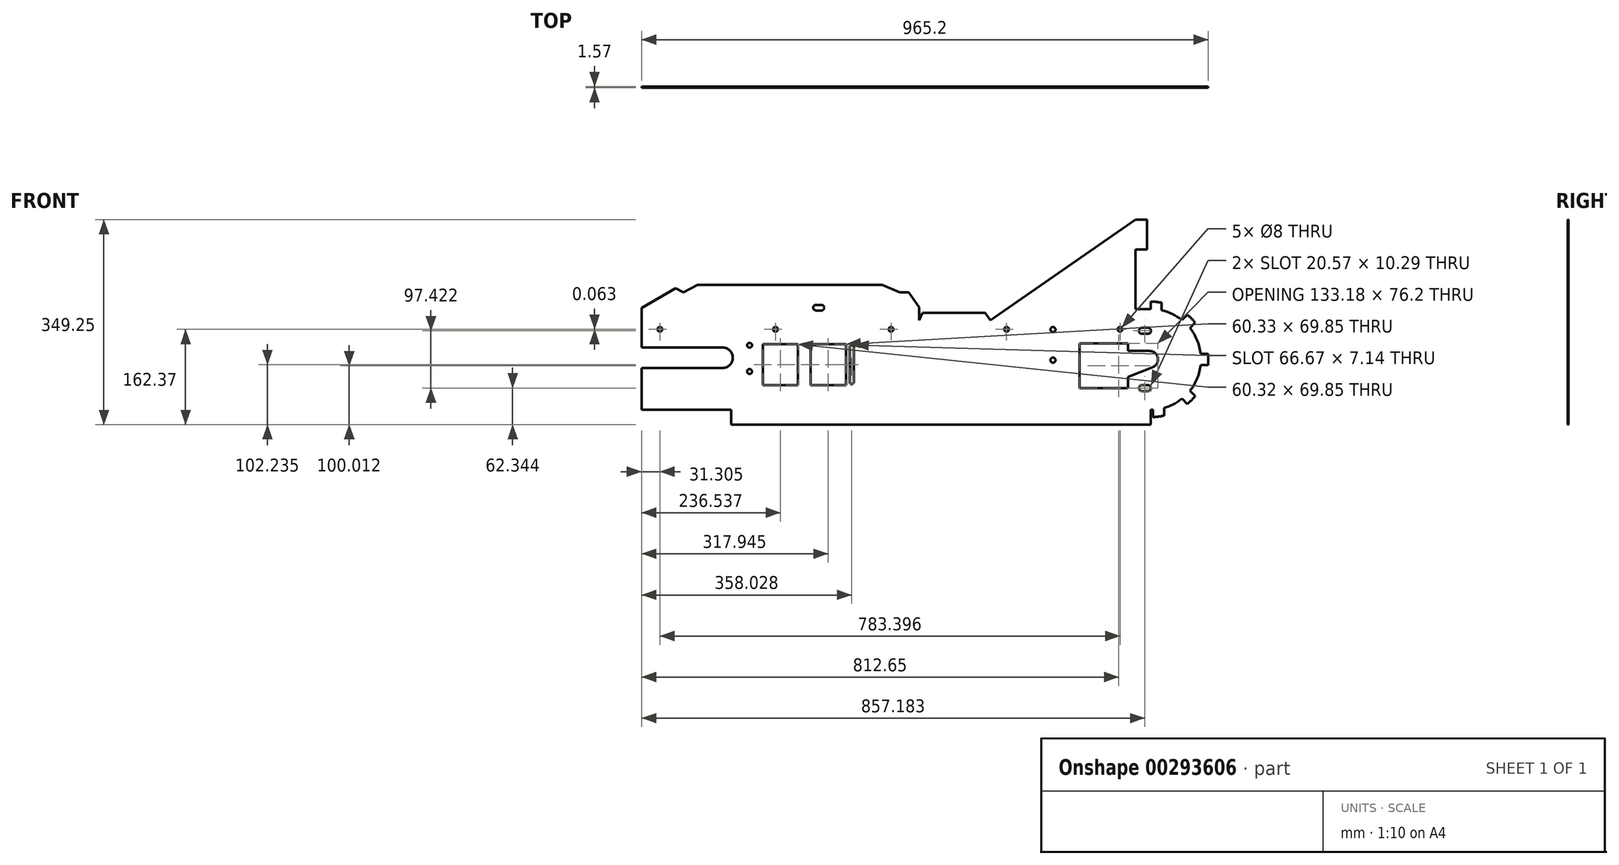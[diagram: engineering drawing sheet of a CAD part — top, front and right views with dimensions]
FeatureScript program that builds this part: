
annotation { "Feature Type Name" : "Feature", "Feature Type Description" : "" }
export const myFeature = defineFeature(function(context is Context, id is Id, definition is map)
    precondition{}
    {
        {
            var Q0;
            Q0=qCreatedBy(makeId("Front.planeOp"),FACE);
            var sketch = newSketch(context, id + "F0", { "sketchPlane" : qUnion([Q0])});
            skLineSegment(sketch, "E0", {"start": v(0, 0) * mm, "end": v(866.78, 0) * mm});
            skLineSegment(sketch, "E1", {"start": v(0, 71.12) * mm, "end": v(138.11, 71.12) * mm});
            skLineSegment(sketch, "E2", {"start": v(138.11, 106.05) * mm, "end": v(0, 106.05) * mm});
            skLineSegment(sketch, "E3", {"start": v(0, 106.05) * mm, "end": v(0, 158.75) * mm});
            skLineSegment(sketch, "E4", {"start": v(0, 158.75) * mm, "end": v(71.5, 200.03) * mm});
            skLineSegment(sketch, "E5", {"start": v(71.5, 200.03) * mm, "end": v(439.73, 200.03) * mm});
            skLineSegment(sketch, "E6", {"start": v(439.73, 200.03) * mm, "end": v(473.08, 152.4) * mm});
            skLineSegment(sketch, "E7", {"start": v(473.08, 152.4) * mm, "end": v(593.73, 152.4) * mm});
            skLineSegment(sketch, "E8", {"start": v(593.73, 152.4) * mm, "end": v(841.38, 323.85) * mm});
            skLineSegment(sketch, "E9", {"start": v(841.38, 323.85) * mm, "end": v(841.38, 171.45) * mm});
            skPoint(sketch, "E10", {"position": v(866.78, 85.73) * mm});
            skArc(sketch, "E11", {"start": v(866.78, 0) * mm, "mid": v(952.5, 85.73) * mm, "end": v(866.78, 171.45) * mm});
            skLineSegment(sketch, "E12", {"start": v(866.78, 171.45) * mm, "end": v(751.67, 171.45) * mm});
            skPoint(sketch, "E13", {"position": v(138.11, 88.58) * mm});
            skPoint(sketch, "E13.positionSnap0", {"position": v(155.58, 88.58) * mm});
            skArc(sketch, "E14", {"start": v(138.11, 71.12) * mm, "mid": v(155.58, 88.58) * mm, "end": v(138.11, 106.04) * mm});
            skLineSegment(sketch, "E15", {"start": v(206.38, 88.58) * mm, "end": v(206.38, 41.91) * mm});
            skLineSegment(sketch, "E16", {"start": v(206.38, 41.91) * mm, "end": v(266.7, 41.91) * mm});
            skLineSegment(sketch, "E17", {"start": v(266.7, 41.91) * mm, "end": v(266.7, 111.76) * mm});
            skLineSegment(sketch, "E18", {"start": v(266.7, 111.76) * mm, "end": v(206.38, 111.76) * mm});
            skLineSegment(sketch, "E19", {"start": v(206.38, 111.76) * mm, "end": v(206.38, 88.58) * mm});
            skLineSegment(sketch, "E20.bottom", {"start": v(287.78, 41.91) * mm, "end": v(348.1, 41.91) * mm});
            skLineSegment(sketch, "E20.top", {"start": v(287.78, 111.76) * mm, "end": v(348.1, 111.76) * mm});
            skLineSegment(sketch, "E20.left", {"start": v(287.78, 41.91) * mm, "end": v(287.78, 111.76) * mm});
            skLineSegment(sketch, "E20.right", {"start": v(348.1, 41.91) * mm, "end": v(348.1, 111.76) * mm});
            skArc(sketch, "E21", {"start": v(354.46, 47.07) * mm, "mid": v(358.08, 43.5) * mm, "end": v(361.6, 47.17) * mm});
            skArc(sketch, "E22", {"start": v(361.6, 106.5) * mm, "mid": v(358.08, 110.17) * mm, "end": v(354.46, 106.6) * mm});
            skLineSegment(sketch, "E23", {"start": v(361.6, 106.7) * mm, "end": v(361.6, 47.07) * mm});
            skLineSegment(sketch, "E24", {"start": v(0, 0) * mm, "end": v(0, 71.12) * mm});
            skLineSegment(sketch, "E25", {"start": v(354.46, 47.07) * mm, "end": v(354.46, 106.6) * mm});
            skPoint(sketch, "E26.orphan", {"position": v(155.58, 106.05) * mm});
            skPoint(sketch, "E27.orphan", {"position": v(155.57, 71.12) * mm});
            skLineSegment(sketch, "E28.bottom", {"start": v(746.06, 36.51) * mm, "end": v(828.6, 36.51) * mm});
            skLineSegment(sketch, "E28.top", {"start": v(746.06, 112.71) * mm, "end": v(828.6, 112.71) * mm});
            skLineSegment(sketch, "E28.left", {"start": v(746.06, 36.51) * mm, "end": v(746.06, 112.71) * mm});
            skLineSegment(sketch, "E28.right", {"start": v(828.6, 36.51) * mm, "end": v(828.6, 55.56) * mm});
            skLineSegment(sketch, "E29", {"start": v(828.6, 100.01) * mm, "end": v(865.12, 100.01) * mm});
            skPoint(sketch, "E30", {"position": v(828.6, 55.56) * mm});
            skPoint(sketch, "E31", {"position": v(865.12, 85.73) * mm});
            skArc(sketch, "E32", {"start": v(870.47, 72.48) * mm, "mid": v(879.15, 88.45) * mm, "end": v(865.12, 100.01) * mm});
            skLineSegment(sketch, "E33", {"start": v(828.6, 55.56) * mm, "end": v(870.47, 72.48) * mm});
            skLineSegment(sketch, "E34.trimOffspring", {"start": v(828.6, 100.01) * mm, "end": v(828.6, 112.71) * mm});
            skLineSegment(sketch, "E35", {"start": v(152.4, 0) * mm, "end": v(152.4, -25.4) * mm});
            skLineSegment(sketch, "E36", {"start": v(152.4, -25.4) * mm, "end": v(866.78, -25.4) * mm});
            skLineSegment(sketch, "E37", {"start": v(866.78, -25.4) * mm, "end": v(866.78, 0) * mm});
            skLineSegment(sketch, "E38", {"start": v(71.5, 200.03) * mm, "end": v(95.54, 212.72) * mm});
            skLineSegment(sketch, "E39", {"start": v(95.54, 212.72) * mm, "end": v(410.03, 212.72) * mm});
            skLineSegment(sketch, "E40", {"start": v(410.03, 212.72) * mm, "end": v(439.73, 200.03) * mm});
            skArc(sketch, "E41.0", {"start": v(871, -12.6) * mm, "mid": v(880.5, -11.74) * mm, "end": v(889.87, -9.95) * mm});
            skLineSegment(sketch, "E42", {"start": v(866.78, 184.15) * mm, "end": v(866.78, 171.45) * mm});
            skLineSegment(sketch, "E43", {"start": v(885.7, 169.33) * mm, "end": v(885.74, 182.3) * mm});
            skLineSegment(sketch, "E44", {"start": v(951.97, 95.25) * mm, "end": v(964.74, 95.25) * mm});
            skLineSegment(sketch, "E45", {"start": v(951.97, 76.2) * mm, "end": v(964.74, 76.2) * mm});
            skLineSegment(sketch, "E46", {"start": v(871, 0.1) * mm, "end": v(871, -12.6) * mm});
            skLineSegment(sketch, "E47", {"start": v(889.81, 3.15) * mm, "end": v(889.87, -9.95) * mm});
            skLineSegment(sketch, "E48", {"start": v(866.78, 85.73) * mm, "end": v(1018.53, 85.73) * mm});
            skLineSegment(sketch, "E49", {"start": v(866.78, 85.72) * mm, "end": v(977.94, 196.9) * mm});
            skLineSegment(sketch, "E50", {"start": v(866.78, 85.73) * mm, "end": v(952.5, 0) * mm});
            skLineSegment(sketch, "E51", {"start": v(920.28, 152.7) * mm, "end": v(929.31, 161.73) * mm});
            skLineSegment(sketch, "E52", {"start": v(933.75, 139.23) * mm, "end": v(942.78, 148.26) * mm});
            skLineSegment(sketch, "E53", {"start": v(933.75, 32.22) * mm, "end": v(942.78, 23.19) * mm});
            skLineSegment(sketch, "E54", {"start": v(920.28, 18.75) * mm, "end": v(929.31, 9.72) * mm});
            skArc(sketch, "E55.trimOffspring", {"start": v(929.31, 9.72) * mm, "mid": v(936.37, 16.13) * mm, "end": v(942.78, 23.19) * mm});
            skArc(sketch, "E56.trimOffspring", {"start": v(964.74, 76.2) * mm, "mid": v(965.08, 80.96) * mm, "end": v(965.2, 85.73) * mm});
            skArc(sketch, "E57.trimOffspring", {"start": v(942.78, 148.26) * mm, "mid": v(936.37, 155.32) * mm, "end": v(929.31, 161.73) * mm});
            skArc(sketch, "E58.trimOffspring", {"start": v(885.74, 182.3) * mm, "mid": v(876.3, 183.69) * mm, "end": v(866.78, 184.15) * mm});
            skLineSegment(sketch, "E59.0", {"start": v(0, 173.41) * mm, "end": v(57.89, 206.84) * mm});
            skLineSegment(sketch, "E60.0", {"start": v(455.23, 200.03) * mm, "end": v(473.08, 174.54) * mm});
            skLineSegment(sketch, "E61.1", {"start": v(478.15, 165.1) * mm, "end": v(584.93, 165.1) * mm});
            skLineSegment(sketch, "E62", {"start": v(71.5, 200.03) * mm, "end": v(57.89, 206.84) * mm});
            skLineSegment(sketch, "E63", {"start": v(0, 158.75) * mm, "end": v(0, 173.41) * mm});
            skLineSegment(sketch, "E64", {"start": v(439.73, 200.03) * mm, "end": v(455.23, 200.03) * mm});
            skLineSegment(sketch, "E65", {"start": v(473.08, 152.4) * mm, "end": v(473.08, 174.54) * mm});
            skLineSegment(sketch, "E66", {"start": v(473.08, 152.4) * mm, "end": v(478.15, 165.1) * mm});
            skLineSegment(sketch, "E67", {"start": v(593.73, 152.4) * mm, "end": v(584.93, 165.1) * mm});
            skLineSegment(sketch, "E68", {"start": v(593.73, 152.4) * mm, "end": v(593.73, 167.85) * mm});
            skLineSegment(sketch, "E69.bottom", {"start": v(841.38, 323.85) * mm, "end": v(860.43, 323.85) * mm});
            skLineSegment(sketch, "E69.top", {"start": v(841.38, 273.05) * mm, "end": v(860.43, 273.05) * mm});
            skLineSegment(sketch, "E69.left", {"start": v(841.38, 323.85) * mm, "end": v(841.38, 273.05) * mm});
            skLineSegment(sketch, "E69.right", {"start": v(860.43, 323.85) * mm, "end": v(860.43, 273.05) * mm});
            skLineSegment(sketch, "E70.bottom", {"start": v(841.38, 171.45) * mm, "end": v(860.43, 171.45) * mm});
            skLineSegment(sketch, "E70.top", {"start": v(841.38, 222.25) * mm, "end": v(860.43, 222.25) * mm});
            skLineSegment(sketch, "E70.left", {"start": v(841.38, 171.45) * mm, "end": v(841.38, 222.25) * mm});
            skLineSegment(sketch, "E70.right", {"start": v(860.43, 171.45) * mm, "end": v(860.43, 222.25) * mm});
            skCircle(sketch, "E71", {"center": v(184.09, 65.09) * mm, "radius": 4.13 * mm});
            skCircle(sketch, "E72", {"center": v(184.09, 109.82) * mm, "radius": 4.13 * mm});
            skCircle(sketch, "E73", {"center": v(228.08, 136.97) * mm, "radius": 4 * mm});
            skLineSegment(sketch, "E74", {"start": v(228.08, 136.97) * mm, "end": v(24.96, 136.97) * mm});
            skCircle(sketch, "E75", {"center": v(31.3, 136.97) * mm, "radius": 4 * mm});
            skLineSegment(sketch, "E76", {"start": v(228.08, 136.97) * mm, "end": v(670.87, 136.97) * mm});
            skCircle(sketch, "E77", {"center": v(424.85, 136.97) * mm, "radius": 4 * mm});
            skCircle(sketch, "E78", {"center": v(621.63, 136.97) * mm, "radius": 4 * mm});
            skCircle(sketch, "E79", {"center": v(306.45, 173.86) * mm, "radius": 4.7 * mm});
            skCircle(sketch, "E80", {"center": v(297.05, 173.86) * mm, "radius": 4.7 * mm});
            skLineSegment(sketch, "E81", {"start": v(306.45, 178.56) * mm, "end": v(297.05, 178.56) * mm});
            skLineSegment(sketch, "E82", {"start": v(306.45, 169.16) * mm, "end": v(297.05, 169.16) * mm});
            skCircle(sketch, "E83", {"center": v(852.04, 134.37) * mm, "radius": 5.14 * mm});
            skCircle(sketch, "E84", {"center": v(852.04, 36.94) * mm, "radius": 5.14 * mm});
            skCircle(sketch, "E85", {"center": v(814.7, 137.03) * mm, "radius": 4 * mm});
            skCircle(sketch, "E86", {"center": v(862.33, 134.37) * mm, "radius": 5.14 * mm});
            skCircle(sketch, "E87", {"center": v(862.33, 36.94) * mm, "radius": 5.14 * mm});
            skLineSegment(sketch, "E88", {"start": v(862.33, 139.5) * mm, "end": v(852.04, 139.5) * mm});
            skLineSegment(sketch, "E89", {"start": v(862.33, 129.22) * mm, "end": v(852.04, 129.22) * mm});
            skLineSegment(sketch, "E90", {"start": v(862.33, 42.09) * mm, "end": v(852.04, 42.09) * mm});
            skLineSegment(sketch, "E91", {"start": v(862.33, 31.8) * mm, "end": v(852.04, 31.8) * mm});
            skCircle(sketch, "E92", {"center": v(700.6, 136.59) * mm, "radius": 4.32 * mm});
            skCircle(sketch, "E93", {"center": v(700.6, 84.52) * mm, "radius": 4.32 * mm});
            skLineSegment(sketch, "E94", {"start": v(965.2, 85.73) * mm, "end": v(964.74, 95.25) * mm});
            skSolve(sketch);
        }
        {
            var Q0;
            Q0=makeQuery(id+"F0.imprint","IMPRINT",FACE,{"disambiguationData":[TD([[makeQuery(id+"F0.imprint","IMPRINT",EDGE,{"derivedFrom":sQuery(id+"F0.wireOp",EDGE,"E1")}),-1.0]])]});
            var Q1;
            {var subQ0=sQuery(id+"F0.wireOp",EDGE,"E11");var subQ8=makeQuery(id+"F0.imprint","INTERSECT",VERTEX,{"derivedFrom":[subQ0,sQuery(id+"F0.wireOp",EDGE,"E44")]});Q1=makeQuery(id+"F0.imprint","IMPRINT",FACE,{"disambiguationData":[TD([[makeQuery(id+"F0.imprint","IMPRINT",EDGE,{"disambiguationData":[TD([[subQ8,1.0]])],"derivedFrom":subQ0}),1.0]])]});}
            var Q2;
            {var subQ5=sQuery(id+"F0.wireOp",EDGE,"E11");var subQ6=makeQuery(id+"F0.imprint","INTERSECT",VERTEX,{"derivedFrom":[subQ5,sQuery(id+"F0.wireOp",EDGE,"E53")]});Q2=makeQuery(id+"F0.imprint","IMPRINT",FACE,{"disambiguationData":[TD([[makeQuery(id+"F0.imprint","IMPRINT",EDGE,{"disambiguationData":[TD([[subQ6,1.0]])],"derivedFrom":subQ5}),1.0]])]});}
            var Q3;
            {var subQ0=sQuery(id+"F0.wireOp",EDGE,"E42");Q3=makeQuery(id+"F0.imprint","IMPRINT",FACE,{"disambiguationData":[TD([[makeQuery(id+"F0.imprint","IMPRINT",EDGE,{"derivedFrom":subQ0}),1.0]])]});}
            var Q4;
            Q4=makeQuery(id+"F0.imprint","IMPRINT",FACE,{"disambiguationData":[TD([[makeQuery(id+"F0.imprint","IMPRINT",EDGE,{"derivedFrom":sQuery(id+"F0.wireOp",EDGE,"E70.bottom")}),1.0]])]});
            var Q5;
            Q5=makeQuery(id+"F0.imprint","IMPRINT",FACE,{"disambiguationData":[TD([[makeQuery(id+"F0.imprint","IMPRINT",EDGE,{"derivedFrom":sQuery(id+"F0.wireOp",EDGE,"E69.bottom")}),-1.0]])]});
            var Q6;
            {var subQ0=sQuery(id+"F0.wireOp",EDGE,"E51");Q6=makeQuery(id+"F0.imprint","IMPRINT",FACE,{"disambiguationData":[TD([[makeQuery(id+"F0.imprint","IMPRINT",EDGE,{"derivedFrom":subQ0}),-1.0]])]});}
            var Q7;
            {var subQ0=sQuery(id+"F0.wireOp",EDGE,"E52");Q7=makeQuery(id+"F0.imprint","IMPRINT",FACE,{"disambiguationData":[TD([[makeQuery(id+"F0.imprint","IMPRINT",EDGE,{"derivedFrom":subQ0}),1.0]])]});}
            var Q8;
            {var subQ0=sQuery(id+"F0.wireOp",EDGE,"E44");Q8=makeQuery(id+"F0.imprint","IMPRINT",FACE,{"disambiguationData":[TD([[makeQuery(id+"F0.imprint","IMPRINT",EDGE,{"derivedFrom":subQ0}),-1.0]])]});}
            var Q9;
            {var subQ0=sQuery(id+"F0.wireOp",EDGE,"E45");Q9=makeQuery(id+"F0.imprint","IMPRINT",FACE,{"disambiguationData":[TD([[makeQuery(id+"F0.imprint","IMPRINT",EDGE,{"derivedFrom":subQ0}),1.0]])]});}
            var Q10;
            {var subQ0=sQuery(id+"F0.wireOp",EDGE,"E53");Q10=makeQuery(id+"F0.imprint","IMPRINT",FACE,{"disambiguationData":[TD([[makeQuery(id+"F0.imprint","IMPRINT",EDGE,{"derivedFrom":subQ0}),-1.0]])]});}
            var Q11;
            {var subQ0=sQuery(id+"F0.wireOp",EDGE,"E54");Q11=makeQuery(id+"F0.imprint","IMPRINT",FACE,{"disambiguationData":[TD([[makeQuery(id+"F0.imprint","IMPRINT",EDGE,{"derivedFrom":subQ0}),1.0]])]});}
            var Q12;
            Q12=makeQuery(id+"F0.imprint","IMPRINT",FACE,{"disambiguationData":[TD([[makeQuery(id+"F0.imprint","IMPRINT",EDGE,{"derivedFrom":sQuery(id+"F0.wireOp",EDGE,"E41.0")}),1.0]])]});
            var Q13;
            {var subQ2=sQuery(id+"F0.wireOp",EDGE,"E35");Q13=makeQuery(id+"F0.imprint","IMPRINT",FACE,{"disambiguationData":[TD([[makeQuery(id+"F0.imprint","IMPRINT",EDGE,{"derivedFrom":subQ2}),1.0]])]});}
            var Q14;
            Q14=makeQuery(id+"F0.imprint","IMPRINT",FACE,{"disambiguationData":[TD([[makeQuery(id+"F0.imprint","IMPRINT",EDGE,{"derivedFrom":sQuery(id+"F0.wireOp",EDGE,"E7")}),1.0]])]});
            var Q15;
            Q15=makeQuery(id+"F0.imprint","IMPRINT",FACE,{"disambiguationData":[TD([[makeQuery(id+"F0.imprint","IMPRINT",EDGE,{"derivedFrom":sQuery(id+"F0.wireOp",EDGE,"E6")}),1.0]])]});
            var Q16;
            Q16=makeQuery(id+"F0.imprint","IMPRINT",FACE,{"disambiguationData":[TD([[makeQuery(id+"F0.imprint","IMPRINT",EDGE,{"derivedFrom":sQuery(id+"F0.wireOp",EDGE,"E5")}),1.0]])]});
            var Q17;
            Q17=makeQuery(id+"F0.imprint","IMPRINT",FACE,{"disambiguationData":[TD([[makeQuery(id+"F0.imprint","IMPRINT",EDGE,{"derivedFrom":sQuery(id+"F0.wireOp",EDGE,"E4")}),1.0]])]});
            extrude(context, id + "F1", {"entities" : qUnion([Q0, Q1, Q2, Q3, Q4, Q5, Q6, Q7, Q8, Q9, Q10, Q11, Q12, Q13, Q14, Q15, Q16, Q17]), "depth" : 1.57 * mm});
        }
        {
            var Q0;
            Q0=makeQuery(id+"F1.opExtrude","CAP_FACE",FACE,{"disambiguationData":[OSD([sQuery(id+"F0.wireOp",EDGE,"E0"),sQuery(id+"F0.wireOp",EDGE,"E1"),sQuery(id+"F0.wireOp",EDGE,"E2"),sQuery(id+"F0.wireOp",EDGE,"E3"),sQuery(id+"F0.wireOp",EDGE,"E8"),sQuery(id+"F0.wireOp",EDGE,"E9"),sQuery(id+"F0.wireOp",EDGE,"E11"),sQuery(id+"F0.wireOp",EDGE,"E12"),sQuery(id+"F0.wireOp",EDGE,"E14"),sQuery(id+"F0.wireOp",EDGE,"E15"),sQuery(id+"F0.wireOp",EDGE,"E16"),sQuery(id+"F0.wireOp",EDGE,"E17"),sQuery(id+"F0.wireOp",EDGE,"E18"),sQuery(id+"F0.wireOp",EDGE,"E19"),sQuery(id+"F0.wireOp",EDGE,"E20.bottom"),sQuery(id+"F0.wireOp",EDGE,"E20.top"),sQuery(id+"F0.wireOp",EDGE,"E20.left"),sQuery(id+"F0.wireOp",EDGE,"E20.right"),sQuery(id+"F0.wireOp",EDGE,"E21"),sQuery(id+"F0.wireOp",EDGE,"E22"),sQuery(id+"F0.wireOp",EDGE,"E23"),sQuery(id+"F0.wireOp",EDGE,"E24"),sQuery(id+"F0.wireOp",EDGE,"E25"),sQuery(id+"F0.wireOp",EDGE,"E28.bottom"),sQuery(id+"F0.wireOp",EDGE,"E28.top"),sQuery(id+"F0.wireOp",EDGE,"E28.left"),sQuery(id+"F0.wireOp",EDGE,"E28.right"),sQuery(id+"F0.wireOp",EDGE,"E29"),sQuery(id+"F0.wireOp",EDGE,"E32"),sQuery(id+"F0.wireOp",EDGE,"E33"),sQuery(id+"F0.wireOp",EDGE,"E34.trimOffspring"),sQuery(id+"F0.wireOp",EDGE,"E35"),sQuery(id+"F0.wireOp",EDGE,"E36"),sQuery(id+"F0.wireOp",EDGE,"E37"),sQuery(id+"F0.wireOp",EDGE,"E38"),sQuery(id+"F0.wireOp",EDGE,"E39"),sQuery(id+"F0.wireOp",EDGE,"E40"),sQuery(id+"F0.wireOp",EDGE,"E41.0"),sQuery(id+"F0.wireOp",EDGE,"E42"),sQuery(id+"F0.wireOp",EDGE,"E43"),sQuery(id+"F0.wireOp",EDGE,"E44"),sQuery(id+"F0.wireOp",EDGE,"E45"),sQuery(id+"F0.wireOp",EDGE,"E46"),sQuery(id+"F0.wireOp",EDGE,"E47"),sQuery(id+"F0.wireOp",EDGE,"E51"),sQuery(id+"F0.wireOp",EDGE,"E52"),sQuery(id+"F0.wireOp",EDGE,"E53"),sQuery(id+"F0.wireOp",EDGE,"E54"),sQuery(id+"F0.wireOp",EDGE,"E55.trimOffspring"),sQuery(id+"F0.wireOp",EDGE,"E56.trimOffspring"),sQuery(id+"F0.wireOp",EDGE,"E57.trimOffspring"),sQuery(id+"F0.wireOp",EDGE,"E58.trimOffspring"),sQuery(id+"F0.wireOp",EDGE,"E59.0"),sQuery(id+"F0.wireOp",EDGE,"E60.0"),sQuery(id+"F0.wireOp",EDGE,"E61.1"),sQuery(id+"F0.wireOp",EDGE,"E62"),sQuery(id+"F0.wireOp",EDGE,"E63"),sQuery(id+"F0.wireOp",EDGE,"E64"),sQuery(id+"F0.wireOp",EDGE,"E65"),sQuery(id+"F0.wireOp",EDGE,"E66"),sQuery(id+"F0.wireOp",EDGE,"E67"),sQuery(id+"F0.wireOp",EDGE,"E69.bottom"),sQuery(id+"F0.wireOp",EDGE,"E69.top"),sQuery(id+"F0.wireOp",EDGE,"E69.right"),sQuery(id+"F0.wireOp",EDGE,"E70.top"),sQuery(id+"F0.wireOp",EDGE,"E70.right"),sQuery(id+"F0.wireOp",EDGE,"E71"),sQuery(id+"F0.wireOp",EDGE,"E72"),sQuery(id+"F0.wireOp",EDGE,"E73"),sQuery(id+"F0.wireOp",EDGE,"E75"),sQuery(id+"F0.wireOp",EDGE,"E77"),sQuery(id+"F0.wireOp",EDGE,"E78"),sQuery(id+"F0.wireOp",EDGE,"E79"),sQuery(id+"F0.wireOp",EDGE,"E80"),sQuery(id+"F0.wireOp",EDGE,"E81"),sQuery(id+"F0.wireOp",EDGE,"E82"),sQuery(id+"F0.wireOp",EDGE,"E83"),sQuery(id+"F0.wireOp",EDGE,"E84"),sQuery(id+"F0.wireOp",EDGE,"E85"),sQuery(id+"F0.wireOp",EDGE,"E86"),sQuery(id+"F0.wireOp",EDGE,"E87"),sQuery(id+"F0.wireOp",EDGE,"E88"),sQuery(id+"F0.wireOp",EDGE,"E89"),sQuery(id+"F0.wireOp",EDGE,"E90"),sQuery(id+"F0.wireOp",EDGE,"E91"),sQuery(id+"F0.wireOp",EDGE,"E92"),sQuery(id+"F0.wireOp",EDGE,"E93"),sQuery(id+"F0.wireOp",EDGE,"E94")])],"isStart":false});
            var sketch = newSketch(context, id + "F2", { "sketchPlane" : qUnion([Q0])});
            skLineSegment(sketch, "E95", {"start": v(860.43, 171.45) * mm, "end": v(841.38, 171.45) * mm});
            skLineSegment(sketch, "E96", {"start": v(841.38, 171.45) * mm, "end": v(841.38, 173.02) * mm});
            skLineSegment(sketch, "E97", {"start": v(841.38, 173.02) * mm, "end": v(860.43, 173.02) * mm});
            skLineSegment(sketch, "E98", {"start": v(860.43, 173.02) * mm, "end": v(860.43, 171.45) * mm});
            skSolve(sketch);
        }
        {
            var Q0;
            Q0=makeQuery(id+"F2.imprint","IMPRINT",FACE,{"disambiguationData":[TD([[makeQuery(id+"F2.imprint","IMPRINT",EDGE,{"derivedFrom":sQuery(id+"F2.wireOp",EDGE,"E95")}),-1.0]])]});
            extrude(context, id + "F3", {"entities" : qUnion([Q0]), "operationType" : NewBodyOperationType.REMOVE, "oppositeDirection" : true, "depth" : 25.4 * mm});
        }
    });
